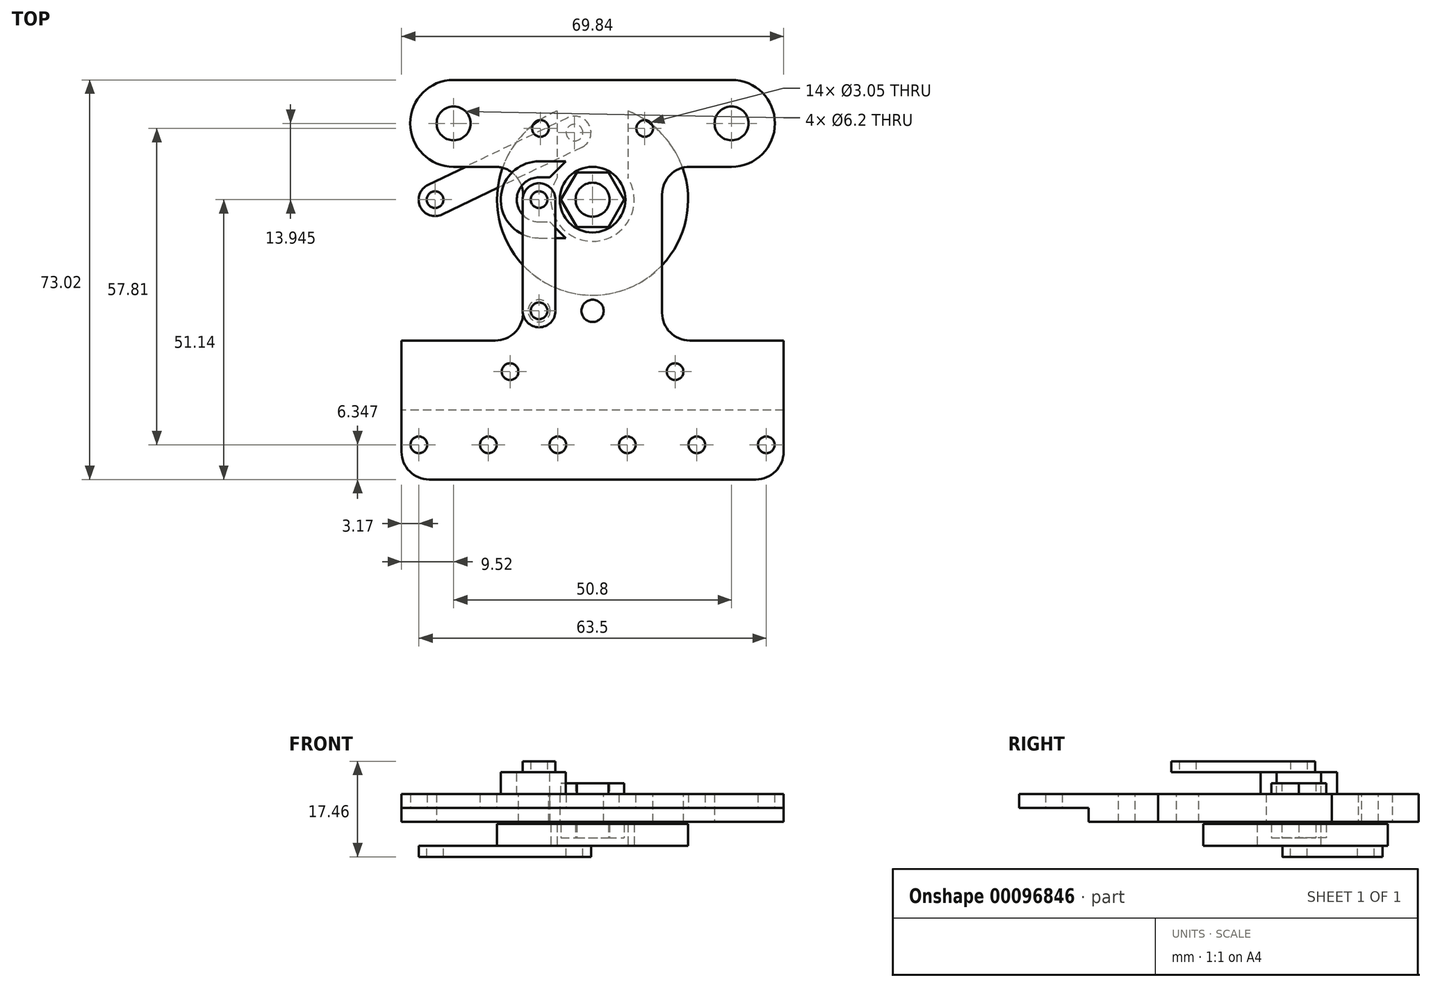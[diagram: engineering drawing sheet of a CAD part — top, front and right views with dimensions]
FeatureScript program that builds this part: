
annotation { "Feature Type Name" : "Feature", "Feature Type Description" : "" }
export const myFeature = defineFeature(function(context is Context, id is Id, definition is map)
    precondition{}
    {
        {
            var Q0;
            Q0=qCreatedBy(makeId("Top.planeOp"),FACE);
            var sketch = newSketch(context, id + "F0", { "sketchPlane" : qUnion([Q0])});
            skLineSegment(sketch, "E0.bottom", {"start": v(-34.92, 36.51) * mm, "end": v(34.93, 36.51) * mm});
            skLineSegment(sketch, "E0.top", {"start": v(-34.93, -36.51) * mm, "end": v(34.92, -36.51) * mm});
            skLineSegment(sketch, "E0.left", {"start": v(-34.92, 36.51) * mm, "end": v(-34.93, -36.51) * mm});
            skLineSegment(sketch, "E0.right", {"start": v(34.93, 36.51) * mm, "end": v(34.92, -36.51) * mm});
            skPoint(sketch, "E0.middle", {"position": v(0, 0) * mm});
            skSolve(sketch);
        }
        {
            var Q0;
            Q0 = qSketchRegion(id + "F0", true);
            extrude(context, id + "F1", {"entities" : qUnion([Q0]), "depth" : 5.08 * mm});
        }
        {
            var Q0;
            Q0=makeQuery(id+"F1.opExtrude","SWEPT_FACE",FACE,{"disambiguationData":[OSD([sQuery(id+"F0.wireOp",EDGE,"E0.left")])]});
            var sketch = newSketch(context, id + "F2", { "sketchPlane" : qUnion([Q0])});
            skLineSegment(sketch, "E1.bottom", {"start": v(36.51, 2.54) * mm, "end": v(23.81, 2.54) * mm});
            skLineSegment(sketch, "E1.top", {"start": v(36.51, 0) * mm, "end": v(23.81, 0) * mm});
            skLineSegment(sketch, "E1.left", {"start": v(36.51, 2.54) * mm, "end": v(36.51, 0) * mm});
            skLineSegment(sketch, "E1.right", {"start": v(23.81, 2.54) * mm, "end": v(23.81, 0) * mm});
            skSolve(sketch);
        }
        {
            var Q0;
            Q0 = qSketchRegion(id + "F2", true);
            extrude(context, id + "F3", {"entities" : qUnion([Q0]), "operationType" : NewBodyOperationType.REMOVE, "endBound" : BoundingType.THROUGH_ALL, "oppositeDirection" : true, "depth" : 25.4 * mm});
        }
        {
            var Q0;
            Q0=makeQuery(id+"F1.opExtrude","CAP_FACE",FACE,{"disambiguationData":[OSD([sQuery(id+"F0.wireOp",EDGE,"E0.bottom"),sQuery(id+"F0.wireOp",EDGE,"E0.top"),sQuery(id+"F0.wireOp",EDGE,"E0.left"),sQuery(id+"F0.wireOp",EDGE,"E0.right")])],"isStart":true});
            var sketch = newSketch(context, id + "F4", { "sketchPlane" : qUnion([Q0])});
            skLineSegment(sketch, "E2", {"start": v(-25.4, -28.58) * mm, "end": v(0, -28.58) * mm, "construction": true});
            skLineSegment(sketch, "E3", {"start": v(0, -28.58) * mm, "end": v(25.4, -28.58) * mm, "construction": true});
            skLineSegment(sketch, "E4", {"start": v(0, -28.58) * mm, "end": v(0, -14.63) * mm, "construction": true});
            skCircle(sketch, "E5", {"center": v(-25.4, -28.58) * mm, "radius": 3.1 * mm});
            skCircle(sketch, "E6", {"center": v(0, -14.63) * mm, "radius": 6 * mm});
            skCircle(sketch, "E7", {"center": v(25.4, -28.58) * mm, "radius": 3.1 * mm});
            skArc(sketch, "E8", {"start": v(-25.4, -36.51) * mm, "mid": v(-33.34, -28.58) * mm, "end": v(-25.4, -20.64) * mm});
            skArc(sketch, "E9", {"start": v(25.4, -36.51) * mm, "mid": v(33.34, -28.58) * mm, "end": v(25.4, -20.64) * mm});
            skLineSegment(sketch, "E10", {"start": v(-25.4, -20.64) * mm, "end": v(-12.7, -20.64) * mm});
            skLineSegment(sketch, "E11", {"start": v(-12.7, -20.64) * mm, "end": v(-12.7, 11.11) * mm});
            skLineSegment(sketch, "E12", {"start": v(-12.7, 11.11) * mm, "end": v(-34.93, 11.11) * mm});
            skLineSegment(sketch, "E13", {"start": v(12.7, 11.11) * mm, "end": v(34.92, 11.11) * mm});
            skLineSegment(sketch, "E14", {"start": v(34.92, 11.11) * mm, "end": v(34.93, -36.51) * mm});
            skLineSegment(sketch, "E15", {"start": v(34.93, -36.51) * mm, "end": v(25.4, -36.51) * mm});
            skLineSegment(sketch, "E16", {"start": v(-25.4, -36.51) * mm, "end": v(-34.92, -36.51) * mm});
            skLineSegment(sketch, "E17", {"start": v(-34.92, -36.51) * mm, "end": v(-34.93, 11.11) * mm});
            skLineSegment(sketch, "E18", {"start": v(25.4, -20.64) * mm, "end": v(12.7, -20.64) * mm});
            skLineSegment(sketch, "E19", {"start": v(12.7, -20.64) * mm, "end": v(12.7, 11.11) * mm});
            skLineSegment(sketch, "E20", {"start": v(-25.4, -28.58) * mm, "end": v(-25.4, -14.63) * mm, "construction": true});
            skLineSegment(sketch, "E21", {"start": v(0, -14.63) * mm, "end": v(-12.7, -14.63) * mm, "construction": true});
            skLineSegment(sketch, "E22", {"start": v(0, -14.63) * mm, "end": v(12.7, -14.63) * mm, "construction": true});
            skSolve(sketch);
        }
        {
            var Q0;
            Q0 = qSketchRegion(id + "F4", true);
            extrude(context, id + "F5", {"entities" : qUnion([Q0]), "operationType" : NewBodyOperationType.REMOVE, "endBound" : BoundingType.UP_TO_NEXT, "oppositeDirection" : true, "depth" : 25.4 * mm});
        }
        {
            var Q0;
            Q0=makeQuery(id+"F5.boolean.opBoolean","COPY",EDGE,{"derivedFrom":makeQuery(id+"F5.opExtrude","SWEPT_EDGE",EDGE,{"disambiguationData":[OSD([sQuery(id+"F4.wireOp",EDGE,"E10"),sQuery(id+"F4.wireOp",EDGE,"E11")])]})});
            var Q1;
            Q1=makeQuery(id+"F5.boolean.opBoolean","COPY",EDGE,{"derivedFrom":makeQuery(id+"F5.opExtrude","SWEPT_EDGE",EDGE,{"disambiguationData":[OSD([sQuery(id+"F4.wireOp",EDGE,"E18"),sQuery(id+"F4.wireOp",EDGE,"E19")])]})});
            var Q2;
            Q2=makeQuery(id+"F5.boolean.opBoolean","COPY",EDGE,{"derivedFrom":makeQuery(id+"F5.opExtrude","SWEPT_EDGE",EDGE,{"disambiguationData":[OSD([sQuery(id+"F4.wireOp",EDGE,"E13"),sQuery(id+"F4.wireOp",EDGE,"E19")])]})});
            var Q3;
            Q3=makeQuery(id+"F5.boolean.opBoolean","COPY",EDGE,{"derivedFrom":makeQuery(id+"F5.opExtrude","SWEPT_EDGE",EDGE,{"disambiguationData":[OSD([sQuery(id+"F4.wireOp",EDGE,"E11"),sQuery(id+"F4.wireOp",EDGE,"E12")])]})});
            var Q4;
            Q4=makeQuery(id+"F5.boolean.opBoolean","COPY",EDGE,{"derivedFrom":makeQuery(id+"F5.opExtrude","SWEPT_EDGE",EDGE,{"disambiguationData":[OSD([sQuery(id+"F0.wireOp",EDGE,"E0.right"),sQuery(id+"F4.wireOp",EDGE,"E13"),sQuery(id+"F4.wireOp",EDGE,"E14")])]})});
            var Q5;
            Q5=makeQuery(id+"F5.boolean.opBoolean","COPY",EDGE,{"derivedFrom":makeQuery(id+"F5.opExtrude","SWEPT_EDGE",EDGE,{"disambiguationData":[OSD([sQuery(id+"F0.wireOp",EDGE,"E0.left"),sQuery(id+"F4.wireOp",EDGE,"E12"),sQuery(id+"F4.wireOp",EDGE,"E17")])]})});
            var Q6;
            Q6=makeQuery(id+"F1.opExtrude","SWEPT_EDGE",EDGE,{"disambiguationData":[OSD([sQuery(id+"F0.wireOp",EDGE,"E0.top"),sQuery(id+"F0.wireOp",EDGE,"E0.left")])]});
            var Q7;
            Q7=makeQuery(id+"F1.opExtrude","SWEPT_EDGE",EDGE,{"disambiguationData":[OSD([sQuery(id+"F0.wireOp",EDGE,"E0.top"),sQuery(id+"F0.wireOp",EDGE,"E0.right")])]});
            fillet(context, id + "F6", {"entities" : qUnion([Q0, Q1, Q2, Q3, Q4, Q5, Q6, Q7]), "radius" : 5.08 * mm, "tangentPropagation" : true, "allowEdgeOverflow" : false});
        }
        {
            var Q0;
            Q0=makeQuery(id+"F1.opExtrude","CAP_FACE",FACE,{"disambiguationData":[OSD([sQuery(id+"F0.wireOp",EDGE,"E0.bottom"),sQuery(id+"F0.wireOp",EDGE,"E0.top"),sQuery(id+"F0.wireOp",EDGE,"E0.left"),sQuery(id+"F0.wireOp",EDGE,"E0.right")])],"isStart":true});
            cPlane(context, id + "F7", {"entities" : qUnion([Q0]), "cplaneType" : CPlaneType.OFFSET, "offset" : 0.38 * mm, "width" : 152.4 * mm, "height" : 152.4 * mm});
        }
        {
            var Q0;
            Q0=qCreatedBy(id+"F7.planeOp",FACE);
            var sketch = newSketch(context, id + "F8", { "sketchPlane" : qUnion([Q0])});
            skCircle(sketch, "E23", {"center": v(0, -14.63) * mm, "radius": 17.46 * mm});
            skSolve(sketch);
        }
        {
            var Q0;
            Q0=makeQuery(id+"F8.imprint","IMPRINT",FACE,{"disambiguationData":[TD([[makeQuery(id+"F8.imprint","IMPRINT",EDGE,{"derivedFrom":sQuery(id+"F8.wireOp",EDGE,"7JbUnUjg-stlZ-eKcx-IOZO-H9E1dYresgRF.bottom")}),-1.0]])]});
            var Q1;
            Q1=makeQuery(id+"F8.imprint","IMPRINT",FACE,{"disambiguationData":[TD([[makeQuery(id+"F8.imprint","IMPRINT",EDGE,{"derivedFrom":sQuery(id+"F8.wireOp",EDGE,"E23")}),1.0]])]});
            var Q2;
            Q2=sQuery(id+"F8.wireOp",EDGE,"7JbUnUjg-stlZ-eKcx-IOZO-H9E1dYresgRF.bottom");
            var Q3;
            Q3=sQuery(id+"F8.wireOp",EDGE,"7JbUnUjg-stlZ-eKcx-IOZO-H9E1dYresgRF.top");
            extrude(context, id + "F9", {"entities" : qUnion([Q0, Q1]), "surfaceEntities" : qUnion([Q2, Q3]), "depth" : 4 * mm});
        }
        {
            var Q0;
            Q0=makeQuery(id+"F9.opExtrude","CAP_FACE",FACE,{"disambiguationData":[OSD([sQuery(id+"F8.wireOp",EDGE,"E23")])],"isStart":false});
            var sketch = newSketch(context, id + "F10", { "sketchPlane" : qUnion([Q0])});
            skCircle(sketch, "E24", {"center": v(0, -14.63) * mm, "radius": 3.1 * mm});
            skSolve(sketch);
        }
        {
            var Q0;
            Q0=makeQuery(id+"F10.imprint","IMPRINT",FACE,{"disambiguationData":[TD([[makeQuery(id+"F10.imprint","IMPRINT",EDGE,{"derivedFrom":sQuery(id+"F10.wireOp",EDGE,"E24")}),1.0]])]});
            extrude(context, id + "F11", {"entities" : qUnion([Q0]), "operationType" : NewBodyOperationType.REMOVE, "oppositeDirection" : true, "depth" : 25.4 * mm});
        }
        {
            var Q0;
            Q0=makeQuery(id+"F9.opExtrude","CAP_FACE",FACE,{"disambiguationData":[OSD([sQuery(id+"F8.wireOp",EDGE,"E23")])],"isStart":false});
            var sketch = newSketch(context, id + "F12", { "sketchPlane" : qUnion([Q0])});
            skCircle(sketch, "E25.cCircle", {"center": v(0, -14.63) * mm, "radius": 5 * mm, "construction": true});
            skLineSegment(sketch, "E25.0", {"start": v(2.89, -9.63) * mm, "end": v(5.77, -14.63) * mm});
            skLineSegment(sketch, "E25.1", {"start": v(5.77, -14.63) * mm, "end": v(2.89, -19.63) * mm});
            skLineSegment(sketch, "E25.2", {"start": v(2.89, -19.63) * mm, "end": v(-2.89, -19.63) * mm});
            skLineSegment(sketch, "E25.3", {"start": v(-2.89, -19.63) * mm, "end": v(-5.77, -14.63) * mm});
            skLineSegment(sketch, "E25.4", {"start": v(-5.77, -14.63) * mm, "end": v(-2.89, -9.63) * mm});
            skLineSegment(sketch, "E25.5", {"start": v(-2.89, -9.63) * mm, "end": v(2.89, -9.63) * mm});
            skPoint(sketch, "E25.0.midPoint", {"position": v(4.33, -12.13) * mm});
            skSolve(sketch);
        }
        {
            var Q0;
            Q0=makeQuery(id+"F3.boolean.opBoolean","COPY",FACE,{"derivedFrom":makeQuery(id+"F3.opExtrude","SWEPT_FACE",FACE,{"disambiguationData":[OSD([sQuery(id+"F2.wireOp",EDGE,"E1.bottom")])]})});
            var sketch = newSketch(context, id + "F13", { "sketchPlane" : qUnion([Q0])});
            skLineSegment(sketch, "E26", {"start": v(-31.75, 30.16) * mm, "end": v(-19.05, 30.16) * mm, "construction": true});
            skLineSegment(sketch, "E27", {"start": v(-19.05, 30.16) * mm, "end": v(-6.35, 30.16) * mm, "construction": true});
            skLineSegment(sketch, "E28", {"start": v(-6.35, 30.16) * mm, "end": v(6.35, 30.16) * mm, "construction": true});
            skLineSegment(sketch, "E29", {"start": v(6.35, 30.16) * mm, "end": v(19.05, 30.16) * mm, "construction": true});
            skLineSegment(sketch, "E30", {"start": v(19.05, 30.16) * mm, "end": v(31.75, 30.16) * mm, "construction": true});
            skLineSegment(sketch, "E31", {"start": v(31.75, 30.16) * mm, "end": v(34.92, 30.16) * mm, "construction": true});
            skLineSegment(sketch, "E32", {"start": v(-31.75, 30.16) * mm, "end": v(-34.93, 30.16) * mm, "construction": true});
            skCircle(sketch, "E33", {"center": v(-31.75, 30.16) * mm, "radius": 1.52 * mm});
            skCircle(sketch, "E34", {"center": v(-19.05, 30.16) * mm, "radius": 1.52 * mm});
            skCircle(sketch, "E35", {"center": v(-6.35, 30.16) * mm, "radius": 1.52 * mm});
            skCircle(sketch, "E36", {"center": v(6.35, 30.16) * mm, "radius": 1.52 * mm});
            skCircle(sketch, "E37", {"center": v(19.05, 30.16) * mm, "radius": 1.52 * mm});
            skCircle(sketch, "E38", {"center": v(31.75, 30.16) * mm, "radius": 1.52 * mm});
            skLineSegment(sketch, "E39", {"start": v(-29.85, 36.51) * mm, "end": v(-29.85, 23.81) * mm, "construction": true});
            skPoint(sketch, "E40", {"position": v(-29.85, 30.16) * mm});
            skSolve(sketch);
        }
        {
            var Q0;
            Q0=makeQuery(id+"F12.imprint","IMPRINT",FACE,{"disambiguationData":[TD([[makeQuery(id+"F12.imprint","IMPRINT",EDGE,{"derivedFrom":sQuery(id+"F12.wireOp",EDGE,"E25.0")}),-1.0]])]});
            extrude(context, id + "F14", {"entities" : qUnion([Q0]), "operationType" : NewBodyOperationType.REMOVE, "oppositeDirection" : true, "depth" : 1.5 * mm});
        }
        {
            var Q0;
            Q0=makeQuery(id+"F9.opExtrude","CAP_FACE",FACE,{"disambiguationData":[OSD([sQuery(id+"F8.wireOp",EDGE,"E23")])],"isStart":false});
            var sketch = newSketch(context, id + "F15", { "sketchPlane" : qUnion([Q0])});
            skLineSegment(sketch, "E41", {"start": v(0, -14.63) * mm, "end": v(-3.29, -26.9) * mm, "construction": true});
            skLineSegment(sketch, "E42", {"start": v(-25.4, -28.58) * mm, "end": v(-25.4, -14.63) * mm, "construction": true});
            skLineSegment(sketch, "E43", {"start": v(-25.4, -14.63) * mm, "end": v(-28.78, -14.63) * mm, "construction": true});
            skLineSegment(sketch, "E44", {"start": v(-28.78, -14.63) * mm, "end": v(-3.29, -26.9) * mm, "construction": true});
            skLineSegment(sketch, "E45", {"start": v(0, -14.63) * mm, "end": v(3.29, -26.9) * mm, "construction": true});
            skCircle(sketch, "E46", {"center": v(-3.29, -26.9) * mm, "radius": 1.52 * mm});
            skCircle(sketch, "E47", {"center": v(3.29, -26.9) * mm, "radius": 1.52 * mm});
            skSolve(sketch);
        }
        {
            var Q0;
            Q0=makeQuery(id+"F15.imprint","IMPRINT",FACE,{"disambiguationData":[TD([[makeQuery(id+"F15.imprint","IMPRINT",EDGE,{"derivedFrom":sQuery(id+"F15.wireOp",EDGE,"E46")}),1.0]])]});
            var Q1;
            Q1=makeQuery(id+"F15.imprint","IMPRINT",FACE,{"disambiguationData":[TD([[makeQuery(id+"F15.imprint","IMPRINT",EDGE,{"derivedFrom":sQuery(id+"F15.wireOp",EDGE,"E47")}),1.0]])]});
            var Q2;
            Q2=sQuery(id+"F15.wireOp",EDGE,"E44");
            var Q3;
            Q3=sQuery(id+"F15.wireOp",EDGE,"E41");
            var Q4;
            Q4=sQuery(id+"F15.wireOp",EDGE,"E45");
            var Q5;
            Q5=sQuery(id+"F15.wireOp",EDGE,"E43");
            var Q6;
            Q6=sQuery(id+"F15.wireOp",EDGE,"E42");
            extrude(context, id + "F16", {"entities" : qUnion([Q0, Q1]), "operationType" : NewBodyOperationType.REMOVE, "surfaceEntities" : qUnion([Q2, Q3, Q4, Q5, Q6]), "endBound" : BoundingType.UP_TO_NEXT, "oppositeDirection" : true, "depth" : 25.4 * mm});
        }
        {
            var Q0;
            Q0=makeQuery(id+"F9.opExtrude","CAP_FACE",FACE,{"disambiguationData":[OSD([sQuery(id+"F8.wireOp",EDGE,"E23")])],"isStart":false});
            var sketch = newSketch(context, id + "F17", { "sketchPlane" : qUnion([Q0])});
            skArc(sketch, "E48", {"start": v(-6.48, -18.64) * mm, "mid": v(0, -7.01) * mm, "end": v(6.48, -18.64) * mm});
            skLineSegment(sketch, "E49", {"start": v(-6.48, -18.64) * mm, "end": v(-6.48, -30.85) * mm});
            skLineSegment(sketch, "E50", {"start": v(6.48, -18.64) * mm, "end": v(6.48, -30.85) * mm});
            skSolve(sketch);
        }
        {
            var Q0;
            Q0 = qSketchRegion(id + "F17", true);
            var Q1;
            Q1=makeQuery(id+"F17.imprint","IMPRINT",FACE,{"disambiguationData":[TD([[makeQuery(id+"F17.imprint","IMPRINT",EDGE,{"derivedFrom":sQuery(id+"F17.wireOp",EDGE,"E48")}),1.0]])]});
            extrude(context, id + "F18", {"entities" : qUnion([Q0, Q1]), "operationType" : NewBodyOperationType.REMOVE, "endBound" : BoundingType.UP_TO_NEXT, "oppositeDirection" : true, "depth" : 25.4 * mm});
        }
        {
            var Q0;
            Q0=makeQuery(id+"F9.opExtrude","CAP_FACE",FACE,{"disambiguationData":[OSD([sQuery(id+"F8.wireOp",EDGE,"E23")])],"isStart":false});
            var sketch = newSketch(context, id + "F19", { "sketchPlane" : qUnion([Q0])});
            skLineSegment(sketch, "E51", {"start": v(-3.29, -26.9) * mm, "end": v(-28.78, -14.63) * mm, "construction": true});
            skLineSegment(sketch, "E52", {"start": v(-28.78, -14.63) * mm, "end": v(-25.4, -14.63) * mm, "construction": true});
            skLineSegment(sketch, "E53", {"start": v(-25.4, -14.63) * mm, "end": v(-25.4, -28.58) * mm, "construction": true});
            skArc(sketch, "E54", {"start": v(-30.08, -17.33) * mm, "mid": v(-31.48, -13.33) * mm, "end": v(-27.48, -11.93) * mm});
            skArc(sketch, "E55", {"start": v(-1.99, -24.2) * mm, "mid": v(-0.58, -28.2) * mm, "end": v(-4.59, -29.6) * mm});
            skLineSegment(sketch, "E56", {"start": v(-1.99, -24.2) * mm, "end": v(-27.48, -11.93) * mm});
            skLineSegment(sketch, "E57", {"start": v(-4.59, -29.6) * mm, "end": v(-30.08, -17.33) * mm});
            skCircle(sketch, "E58", {"center": v(-3.29, -26.9) * mm, "radius": 1.52 * mm});
            skCircle(sketch, "E59", {"center": v(-28.78, -14.63) * mm, "radius": 1.52 * mm});
            skSolve(sketch);
        }
        {
            var Q0;
            Q0 = qSketchRegion(id + "F19", true);
            extrude(context, id + "F20", {"entities" : qUnion([Q0]), "depth" : 2 * mm});
        }
        {
            var Q0;
            Q0=makeQuery(id+"F13.imprint","IMPRINT",FACE,{"disambiguationData":[TD([[makeQuery(id+"F13.imprint","IMPRINT",EDGE,{"derivedFrom":sQuery(id+"F13.wireOp",EDGE,"E33")}),1.0]])]});
            var Q1;
            Q1=makeQuery(id+"F13.imprint","IMPRINT",FACE,{"disambiguationData":[TD([[makeQuery(id+"F13.imprint","IMPRINT",EDGE,{"derivedFrom":sQuery(id+"F13.wireOp",EDGE,"E34")}),1.0]])]});
            var Q2;
            Q2=makeQuery(id+"F13.imprint","IMPRINT",FACE,{"disambiguationData":[TD([[makeQuery(id+"F13.imprint","IMPRINT",EDGE,{"derivedFrom":sQuery(id+"F13.wireOp",EDGE,"E35")}),1.0]])]});
            var Q3;
            Q3=makeQuery(id+"F13.imprint","IMPRINT",FACE,{"disambiguationData":[TD([[makeQuery(id+"F13.imprint","IMPRINT",EDGE,{"derivedFrom":sQuery(id+"F13.wireOp",EDGE,"E36")}),1.0]])]});
            var Q4;
            Q4=makeQuery(id+"F13.imprint","IMPRINT",FACE,{"disambiguationData":[TD([[makeQuery(id+"F13.imprint","IMPRINT",EDGE,{"derivedFrom":sQuery(id+"F13.wireOp",EDGE,"E37")}),1.0]])]});
            var Q5;
            Q5=makeQuery(id+"F13.imprint","IMPRINT",FACE,{"disambiguationData":[TD([[makeQuery(id+"F13.imprint","IMPRINT",EDGE,{"derivedFrom":sQuery(id+"F13.wireOp",EDGE,"E38")}),1.0]])]});
            extrude(context, id + "F21", {"entities" : qUnion([Q0, Q1, Q2, Q3, Q4, Q5]), "operationType" : NewBodyOperationType.REMOVE, "endBound" : BoundingType.UP_TO_NEXT, "oppositeDirection" : true, "depth" : 25.4 * mm});
        }
        {
            var Q0;
            Q0=makeQuery(id+"F1.opExtrude","CAP_FACE",FACE,{"disambiguationData":[OSD([sQuery(id+"F0.wireOp",EDGE,"E0.bottom"),sQuery(id+"F0.wireOp",EDGE,"E0.top"),sQuery(id+"F0.wireOp",EDGE,"E0.left"),sQuery(id+"F0.wireOp",EDGE,"E0.right")])],"isStart":false});
            var sketch = newSketch(context, id + "F22", { "sketchPlane" : qUnion([Q0])});
            skCircle(sketch, "E60", {"center": v(0, 14.63) * mm, "radius": 3.1 * mm});
            skCircle(sketch, "E61", {"center": v(-9.78, 14.63) * mm, "radius": 1.52 * mm});
            skLineSegment(sketch, "E62", {"start": v(-9.78, 14.63) * mm, "end": v(0, 14.63) * mm, "construction": true});
            skLineSegment(sketch, "E63.bottom", {"start": v(-9.78, 21.63) * mm, "end": v(0, 21.63) * mm});
            skLineSegment(sketch, "E63.top", {"start": v(-9.78, 7.63) * mm, "end": v(0, 7.63) * mm});
            skLineSegment(sketch, "E63.left", {"start": v(-9.78, 21.63) * mm, "end": v(-9.78, 7.63) * mm, "construction": true});
            skLineSegment(sketch, "E63.right", {"start": v(0, 21.63) * mm, "end": v(0, 7.63) * mm, "construction": true});
            skPoint(sketch, "E63.middle", {"position": v(-4.89, 14.63) * mm});
            skArc(sketch, "E64", {"start": v(-9.78, 7.63) * mm, "mid": v(-16.78, 14.63) * mm, "end": v(-9.78, 21.63) * mm});
            skArc(sketch, "E65", {"start": v(0, 21.63) * mm, "mid": v(7, 14.63) * mm, "end": v(0, 7.63) * mm});
            skSolve(sketch);
        }
        {
            var Q0;
            Q0 = qSketchRegion(id + "F22", true);
            extrude(context, id + "F23", {"entities" : qUnion([Q0]), "depth" : 4 * mm});
        }
        {
            var Q0;
            Q0=makeQuery(id+"F23.opExtrude","CAP_FACE",FACE,{"disambiguationData":[OSD([sQuery(id+"F22.wireOp",EDGE,"E60"),sQuery(id+"F22.wireOp",EDGE,"E61"),sQuery(id+"F22.wireOp",EDGE,"E63.bottom"),sQuery(id+"F22.wireOp",EDGE,"E63.top"),sQuery(id+"F22.wireOp",EDGE,"E64"),sQuery(id+"F22.wireOp",EDGE,"E65")])],"isStart":false});
            var sketch = newSketch(context, id + "F24", { "sketchPlane" : qUnion([Q0])});
            skCircle(sketch, "E66.cCircle", {"center": v(0, 14.63) * mm, "radius": 5 * mm, "construction": true});
            skLineSegment(sketch, "E66.0", {"start": v(-2.89, 19.63) * mm, "end": v(2.89, 19.63) * mm});
            skLineSegment(sketch, "E66.1", {"start": v(2.89, 19.63) * mm, "end": v(5.77, 14.63) * mm});
            skLineSegment(sketch, "E66.2", {"start": v(5.77, 14.63) * mm, "end": v(2.89, 9.63) * mm});
            skLineSegment(sketch, "E66.3", {"start": v(2.89, 9.63) * mm, "end": v(-2.89, 9.63) * mm});
            skLineSegment(sketch, "E66.4", {"start": v(-2.89, 9.63) * mm, "end": v(-5.77, 14.63) * mm});
            skLineSegment(sketch, "E66.5", {"start": v(-5.77, 14.63) * mm, "end": v(-2.89, 19.63) * mm});
            skPoint(sketch, "E66.0.midPoint", {"position": v(0, 19.63) * mm});
            skSolve(sketch);
        }
        {
            var Q0;
            Q0 = qSketchRegion(id + "F24", true);
            extrude(context, id + "F25", {"entities" : qUnion([Q0]), "operationType" : NewBodyOperationType.REMOVE, "oppositeDirection" : true, "depth" : 2 * mm});
        }
        {
            var Q0;
            Q0=makeQuery(id+"F23.opExtrude","CAP_FACE",FACE,{"disambiguationData":[OSD([sQuery(id+"F22.wireOp",EDGE,"E60"),sQuery(id+"F22.wireOp",EDGE,"E61"),sQuery(id+"F22.wireOp",EDGE,"E63.bottom"),sQuery(id+"F22.wireOp",EDGE,"E63.top"),sQuery(id+"F22.wireOp",EDGE,"E64"),sQuery(id+"F22.wireOp",EDGE,"E65")])],"isStart":false});
            var sketch = newSketch(context, id + "F26", { "sketchPlane" : qUnion([Q0])});
            skArc(sketch, "E67", {"start": v(-9.78, 10.57) * mm, "mid": v(-13.84, 14.63) * mm, "end": v(-9.78, 18.7) * mm});
            skLineSegment(sketch, "E68", {"start": v(-9.78, 18.7) * mm, "end": v(-7.83, 18.7) * mm});
            skLineSegment(sketch, "E69", {"start": v(-7.83, 18.7) * mm, "end": v(-4.89, 21.63) * mm});
            skLineSegment(sketch, "E70", {"start": v(-9.78, 10.57) * mm, "end": v(-7.83, 10.57) * mm});
            skLineSegment(sketch, "E71", {"start": v(-7.83, 10.57) * mm, "end": v(-4.89, 7.63) * mm});
            skSolve(sketch);
        }
        {
            var Q0;
            Q0 = qSketchRegion(id + "F26", true);
            var Q1;
            Q1=makeQuery(id+"F26.imprint","IMPRINT",FACE,{"disambiguationData":[TD([[makeQuery(id+"F26.imprint","IMPRINT",EDGE,{"derivedFrom":sQuery(id+"F26.wireOp",EDGE,"E67")}),1.0]])]});
            extrude(context, id + "F27", {"entities" : qUnion([Q0, Q1]), "operationType" : NewBodyOperationType.REMOVE, "endBound" : BoundingType.UP_TO_NEXT, "oppositeDirection" : true, "depth" : 25.4 * mm});
        }
        {
            var Q0;
            Q0=makeQuery(id+"F1.opExtrude","CAP_FACE",FACE,{"disambiguationData":[OSD([sQuery(id+"F0.wireOp",EDGE,"E0.bottom"),sQuery(id+"F0.wireOp",EDGE,"E0.top"),sQuery(id+"F0.wireOp",EDGE,"E0.left"),sQuery(id+"F0.wireOp",EDGE,"E0.right")])],"isStart":false});
            var sketch = newSketch(context, id + "F28", { "sketchPlane" : qUnion([Q0])});
            skCircle(sketch, "E72", {"center": v(0, -5.69) * mm, "radius": 2.03 * mm});
            skLineSegment(sketch, "E73", {"start": v(0, 14.63) * mm, "end": v(0, -5.69) * mm, "construction": true});
            skCircle(sketch, "E74", {"center": v(-9.78, -5.69) * mm, "radius": 2.03 * mm});
            skLineSegment(sketch, "E75", {"start": v(-9.78, -5.69) * mm, "end": v(-9.78, 14.63) * mm, "construction": true});
            skSolve(sketch);
        }
        {
            var Q0;
            Q0 = qSketchRegion(id + "F28", true);
            extrude(context, id + "F29", {"entities" : qUnion([Q0]), "operationType" : NewBodyOperationType.REMOVE, "endBound" : BoundingType.UP_TO_NEXT, "oppositeDirection" : true, "depth" : 25.4 * mm});
        }
        {
            var Q0;
            Q0=makeQuery(id+"F1.opExtrude","CAP_FACE",FACE,{"disambiguationData":[OSD([sQuery(id+"F0.wireOp",EDGE,"E0.bottom"),sQuery(id+"F0.wireOp",EDGE,"E0.top"),sQuery(id+"F0.wireOp",EDGE,"E0.left"),sQuery(id+"F0.wireOp",EDGE,"E0.right")])],"isStart":false});
            var sketch = newSketch(context, id + "F30", { "sketchPlane" : qUnion([Q0])});
            skLineSegment(sketch, "E76.bottom", {"start": v(15.08, 27.65) * mm, "end": v(-15.08, 27.65) * mm, "construction": true});
            skLineSegment(sketch, "E76.top", {"start": v(15.08, -16.8) * mm, "end": v(-15.08, -16.8) * mm, "construction": true});
            skLineSegment(sketch, "E76.left", {"start": v(15.08, 27.65) * mm, "end": v(15.08, -16.8) * mm, "construction": true});
            skLineSegment(sketch, "E76.right", {"start": v(-15.08, 27.65) * mm, "end": v(-15.08, -16.8) * mm, "construction": true});
            skPoint(sketch, "E76.middle", {"position": v(0, 5.42) * mm});
            skLineSegment(sketch, "E77", {"start": v(0, -5.69) * mm, "end": v(0, 5.42) * mm, "construction": true});
            skCircle(sketch, "E78", {"center": v(15.08, -16.8) * mm, "radius": 1.52 * mm});
            skCircle(sketch, "E79", {"center": v(-15.08, -16.8) * mm, "radius": 1.52 * mm});
            skLineSegment(sketch, "E80", {"start": v(-15.08, -16.8) * mm, "end": v(-9.53, 27.65) * mm, "construction": true});
            skLineSegment(sketch, "E81", {"start": v(-9.53, 27.65) * mm, "end": v(0, -16.8) * mm, "construction": true});
            skLineSegment(sketch, "E82", {"start": v(0, -16.8) * mm, "end": v(9.52, 27.65) * mm, "construction": true});
            skLineSegment(sketch, "E83", {"start": v(9.52, 27.65) * mm, "end": v(15.08, -16.8) * mm, "construction": true});
            skCircle(sketch, "E84", {"center": v(-9.53, 27.65) * mm, "radius": 1.52 * mm});
            skCircle(sketch, "E85", {"center": v(9.52, 27.65) * mm, "radius": 1.52 * mm});
            skSolve(sketch);
        }
        {
            var Q0;
            Q0 = qSketchRegion(id + "F30", true);
            extrude(context, id + "F31", {"entities" : qUnion([Q0]), "operationType" : NewBodyOperationType.REMOVE, "endBound" : BoundingType.UP_TO_NEXT, "oppositeDirection" : true, "depth" : 25.4 * mm});
        }
        {
            var Q0;
            Q0=makeQuery(id+"F23.opExtrude","CAP_FACE",FACE,{"disambiguationData":[OSD([sQuery(id+"F22.wireOp",EDGE,"E60"),sQuery(id+"F22.wireOp",EDGE,"E61"),sQuery(id+"F22.wireOp",EDGE,"E63.bottom"),sQuery(id+"F22.wireOp",EDGE,"E63.top"),sQuery(id+"F22.wireOp",EDGE,"E64"),sQuery(id+"F22.wireOp",EDGE,"E65")])],"isStart":true});
            var sketch = newSketch(context, id + "F32", { "sketchPlane" : qUnion([Q0])});
            skCircle(sketch, "E86", {"center": v(-9.78, -14.63) * mm, "radius": 2.8 * mm});
            skSolve(sketch);
        }
        {
            var Q0;
            Q0 = qSketchRegion(id + "F32", true);
            extrude(context, id + "F33", {"entities" : qUnion([Q0]), "operationType" : NewBodyOperationType.REMOVE, "oppositeDirection" : true, "depth" : 2.54 * mm});
        }
        {
            var Q0;
            Q0=makeQuery(id+"F9.opExtrude","CAP_FACE",FACE,{"disambiguationData":[OSD([sQuery(id+"F8.wireOp",EDGE,"E23")])],"isStart":true});
            var sketch = newSketch(context, id + "F34", { "sketchPlane" : qUnion([Q0])});
            skCircle(sketch, "E87", {"center": v(-3.29, 26.9) * mm, "radius": 2.8 * mm});
            skCircle(sketch, "E88", {"center": v(3.29, 26.9) * mm, "radius": 2.8 * mm});
            skSolve(sketch);
        }
        {
            var Q0;
            Q0 = qSketchRegion(id + "F34", true);
            extrude(context, id + "F35", {"entities" : qUnion([Q0]), "operationType" : NewBodyOperationType.REMOVE, "oppositeDirection" : true, "depth" : 2.54 * mm});
        }
        {
            var Q0;
            Q0=makeQuery(id+"F23.opExtrude","CAP_FACE",FACE,{"disambiguationData":[OSD([sQuery(id+"F22.wireOp",EDGE,"E60"),sQuery(id+"F22.wireOp",EDGE,"E61"),sQuery(id+"F22.wireOp",EDGE,"E63.bottom"),sQuery(id+"F22.wireOp",EDGE,"E63.top"),sQuery(id+"F22.wireOp",EDGE,"E64"),sQuery(id+"F22.wireOp",EDGE,"E65")])],"isStart":false});
            var sketch = newSketch(context, id + "F36", { "sketchPlane" : qUnion([Q0])});
            skArc(sketch, "E89", {"start": v(-6.78, 14.63) * mm, "mid": v(-9.78, 17.63) * mm, "end": v(-12.78, 14.63) * mm});
            skArc(sketch, "E90", {"start": v(-12.78, -5.69) * mm, "mid": v(-9.78, -8.69) * mm, "end": v(-6.78, -5.69) * mm});
            skLineSegment(sketch, "E91", {"start": v(-12.78, -5.69) * mm, "end": v(-12.78, 14.63) * mm});
            skLineSegment(sketch, "E92", {"start": v(-6.78, -5.69) * mm, "end": v(-6.78, 14.63) * mm});
            skCircle(sketch, "E93", {"center": v(-9.78, 14.63) * mm, "radius": 1.52 * mm});
            skCircle(sketch, "E94", {"center": v(-9.78, -5.69) * mm, "radius": 1.52 * mm});
            skSolve(sketch);
        }
        {
            var Q0;
            Q0 = qSketchRegion(id + "F36", true);
            extrude(context, id + "F37", {"entities" : qUnion([Q0]), "depth" : 2 * mm});
        }
    });
